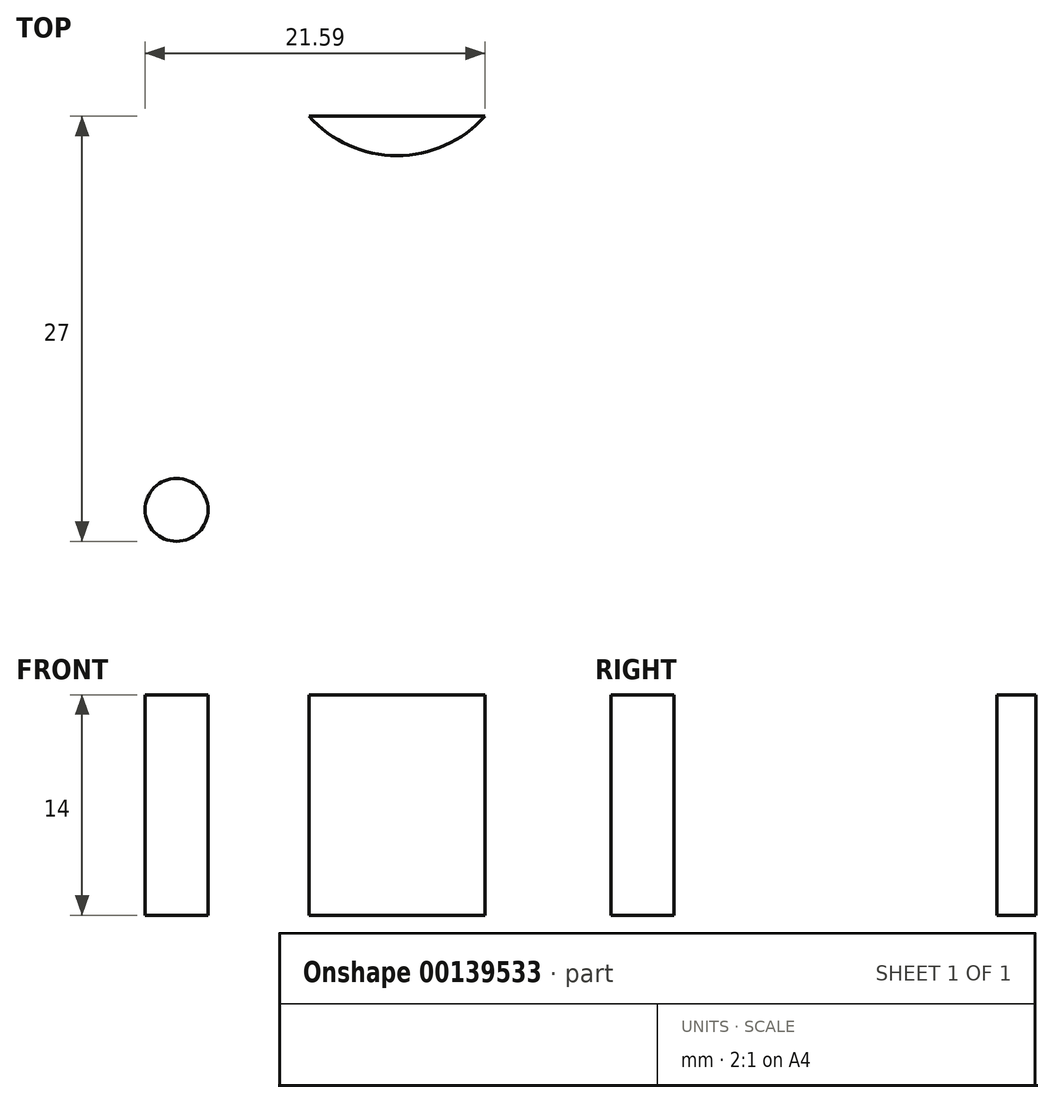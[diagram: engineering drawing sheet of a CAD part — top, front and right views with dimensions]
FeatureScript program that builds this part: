
annotation { "Feature Type Name" : "Feature", "Feature Type Description" : "" }
export const myFeature = defineFeature(function(context is Context, id is Id, definition is map)
    precondition{}
    {
        {
            var Q0;
            Q0=qCreatedBy(makeId("Top.planeOp"),FACE);
            var sketch = newSketch(context, id + "F0", { "sketchPlane" : qUnion([Q0])});
            skLineSegment(sketch, "E0.bottom", {"start": v(30, -20) * mm, "end": v(-30, -20) * mm});
            skLineSegment(sketch, "E0.top", {"start": v(30, 20) * mm, "end": v(-30, 20) * mm});
            skLineSegment(sketch, "E0.left", {"start": v(30, -20) * mm, "end": v(30, 20) * mm});
            skLineSegment(sketch, "E0.right", {"start": v(-30, -20) * mm, "end": v(-30, 20) * mm});
            skPoint(sketch, "E0.middle", {"position": v(0, 0) * mm});
            skSolve(sketch);
        }
        {
            var Q0;
            Q0 = qSketchRegion(id + "F0", true);
            extrude(context, id + "F1", {"entities" : qUnion([Q0]), "oppositeDirection" : true, "depth" : 14 * mm});
        }
        {
            var Q0;
            Q0=makeQuery(id+"F1.opExtrude","CAP_FACE",FACE,{"disambiguationData":[OSD([sQuery(id+"F0.wireOp",EDGE,"E0.bottom"),sQuery(id+"F0.wireOp",EDGE,"E0.top"),sQuery(id+"F0.wireOp",EDGE,"E0.left"),sQuery(id+"F0.wireOp",EDGE,"E0.right")])],"isStart":true});
            var sketch = newSketch(context, id + "F2", { "sketchPlane" : qUnion([Q0])});
            skPoint(sketch, "E1.centerSnap0", {"position": v(0, 20) * mm});
            skCircle(sketch, "E2", {"center": v(0, -5) * mm, "radius": 10 * mm});
            skLineSegment(sketch, "E3", {"start": v(0, -5) * mm, "end": v(114.16, -5) * mm, "construction": true});
            skCircle(sketch, "E4", {"center": v(14, -5) * mm, "radius": 2 * mm});
            skCircle(sketch, "E5.MirrorC", {"center": v(-14, -5) * mm, "radius": 2 * mm});
            skCircle(sketch, "E6", {"center": v(0, 25) * mm, "radius": 7.5 * mm});
            skSolve(sketch);
        }
        {
            var Q0;
            Q0=sQuery(id+"F2.wireOp",EDGE,"E6");
            extrude(context, id + "F3", {"bodyType" : ToolBodyType.SURFACE, "surfaceEntities" : qUnion([Q0]), "depth" : 36 * mm, "hasSecondDirection" : true, "secondDirectionOppositeDirection" : true, "secondDirectionDepth" : 14 * mm});
        }
        {
            var Q0;
            Q0=makeQuery(id+"F2.imprint","IMPRINT",FACE,{"disambiguationData":[TD([[makeQuery(id+"F2.imprint","IMPRINT",EDGE,{"derivedFrom":sQuery(id+"F2.wireOp",EDGE,"E2")}),1.0]])]});
            var Q1;
            Q1=makeQuery(id+"F2.imprint","IMPRINT",FACE,{"disambiguationData":[TD([[makeQuery(id+"F2.imprint","IMPRINT",EDGE,{"derivedFrom":sQuery(id+"F2.wireOp",EDGE,"E5.MirrorC")}),-1.0]])]});
            var Q2;
            Q2=makeQuery(id+"F2.imprint","IMPRINT",FACE,{"disambiguationData":[TD([[makeQuery(id+"F2.imprint","IMPRINT",EDGE,{"derivedFrom":sQuery(id+"F2.wireOp",EDGE,"E4")}),1.0]])]});
            extrude(context, id + "F4", {"entities" : qUnion([Q0, Q1, Q2]), "operationType" : NewBodyOperationType.REMOVE, "endBound" : BoundingType.UP_TO_NEXT, "oppositeDirection" : true, "depth" : 25 * mm});
        }
    });
